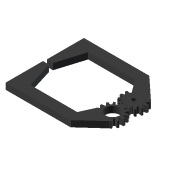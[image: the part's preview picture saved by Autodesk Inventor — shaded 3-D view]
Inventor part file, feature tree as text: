
AUTODESK INVENTOR PART (.ipt)
format: ipt  version: 2021 (Build 250183000, 183)  size: 251,392 bytes
history: native  units: mm
features: other x1, extrude x1, sketch x1
ambient origin geometry x8: Origin, YZ Plane, XZ Plane, XY Plane, X Axis, Y Axis, Z Axis, Center Point
bodies: Body1 (feature_tree)
feature tree (3):
  other  "Sólido1"
  extrude  "Extrusión1"  Depth=4.0mm
  sketch  "Boceto1"  dims[d1=9.0mm d2=11.0mm d3=15.0mm d9=140.0mm d11=360.0deg d16=20.0mm d19=30.0mm d21=140.0mm d30=6.3mm d31=3.0mm d32=4.0mm d33=0.0mm]
